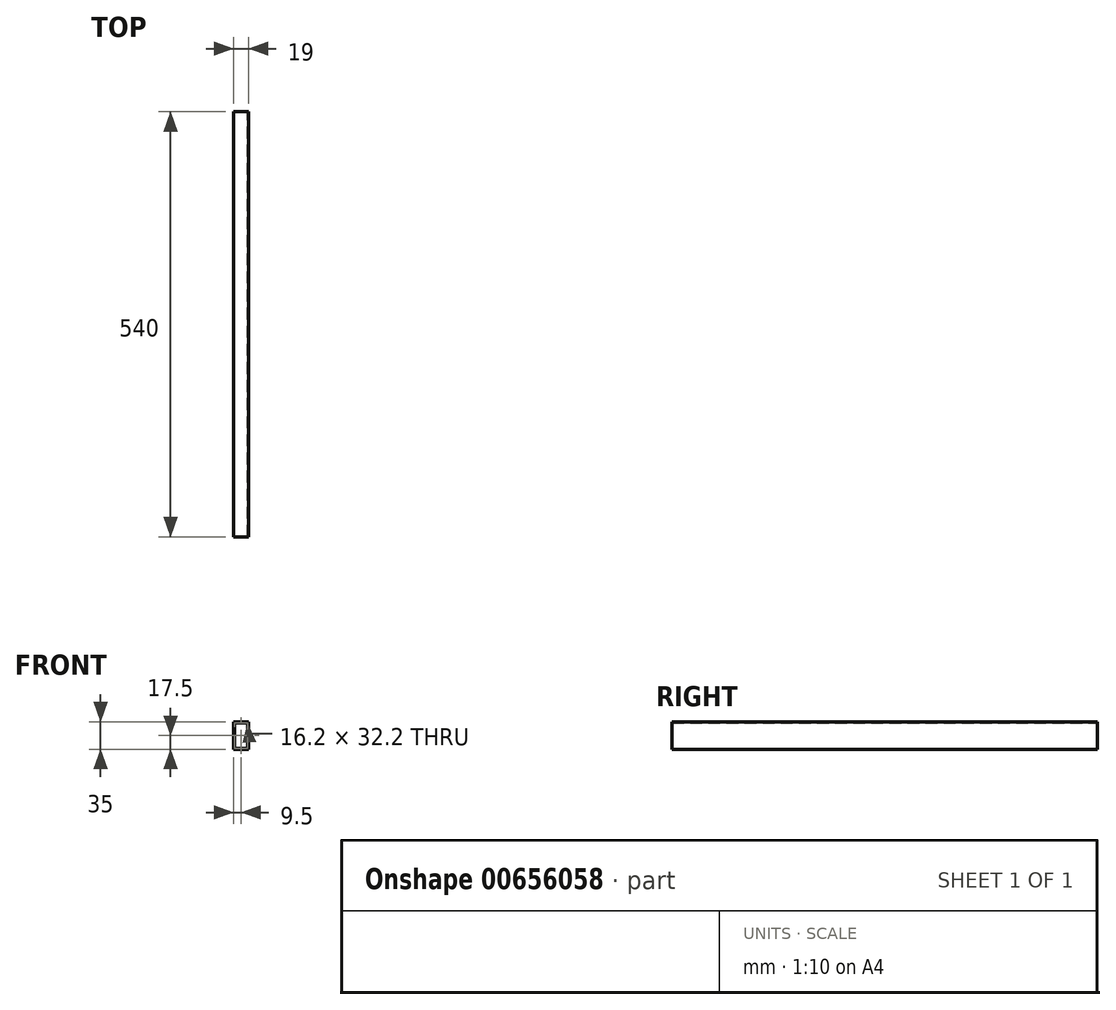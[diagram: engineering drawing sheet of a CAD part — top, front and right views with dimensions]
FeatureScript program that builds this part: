
annotation { "Feature Type Name" : "Feature", "Feature Type Description" : "" }
export const myFeature = defineFeature(function(context is Context, id is Id, definition is map)
    precondition{}
    {
        {
            var Q0;
            Q0=qCreatedBy(makeId("Front.planeOp"),FACE);
            var sketch = newSketch(context, id + "F0", { "sketchPlane" : qUnion([Q0])});
            skLineSegment(sketch, "E0.bottom", {"start": v(0, 0) * mm, "end": v(19, 0) * mm});
            skLineSegment(sketch, "E0.top", {"start": v(0, -35) * mm, "end": v(19, -35) * mm});
            skLineSegment(sketch, "E0.left", {"start": v(0, 0) * mm, "end": v(0, -35) * mm});
            skLineSegment(sketch, "E0.right", {"start": v(19, 0) * mm, "end": v(19, -35) * mm});
            skLineSegment(sketch, "E1.0", {"start": v(1.4, -1.4) * mm, "end": v(17.6, -1.4) * mm});
            skLineSegment(sketch, "E1.1", {"start": v(1.4, -1.4) * mm, "end": v(1.4, -33.6) * mm});
            skLineSegment(sketch, "E1.2", {"start": v(1.4, -33.6) * mm, "end": v(17.6, -33.6) * mm});
            skLineSegment(sketch, "E1.3", {"start": v(17.6, -1.4) * mm, "end": v(17.6, -33.6) * mm});
            skSolve(sketch);
        }
        {
            var Q0;
            Q0=makeQuery(id+"F0.imprint","IMPRINT",FACE,{"disambiguationData":[TD([[makeQuery(id+"F0.imprint","IMPRINT",EDGE,{"derivedFrom":sQuery(id+"F0.wireOp",EDGE,"E0.bottom")}),-1.0]])]});
            extrude(context, id + "F1", {"entities" : qUnion([Q0]), "depth" : 540 * mm, "offsetDistance" : 25.4 * mm});
        }
    });
